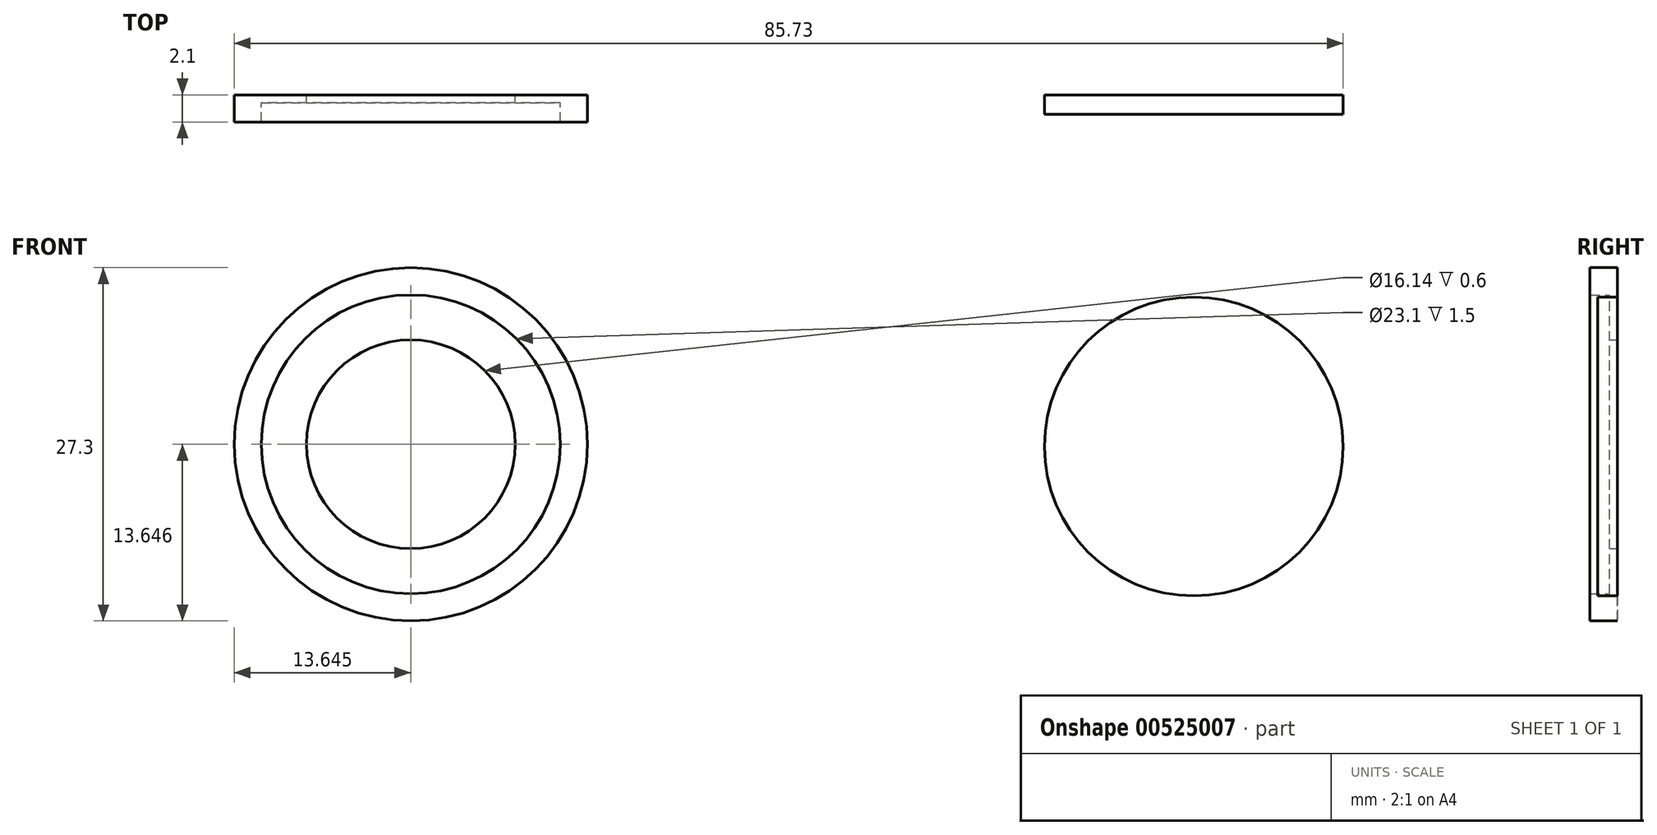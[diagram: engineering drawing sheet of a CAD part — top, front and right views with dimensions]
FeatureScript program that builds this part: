
annotation { "Feature Type Name" : "Feature", "Feature Type Description" : "" }
export const myFeature = defineFeature(function(context is Context, id is Id, definition is map)
    precondition{}
    {
        {
            var Q0;
            Q0=qCreatedBy(makeId("Front.planeOp"),FACE);
            var sketch = newSketch(context, id + "F0", { "sketchPlane" : qUnion([Q0])});
            skCircle(sketch, "E0", {"center": v(-41.74, 19.38) * mm, "radius": 13.65 * mm});
            skCircle(sketch, "E1", {"center": v(-41.74, 19.38) * mm, "radius": 11.55 * mm});
            skCircle(sketch, "E2", {"center": v(-41.74, 19.38) * mm, "radius": 8.07 * mm});
            skSolve(sketch);
        }
        {
            var Q0;
            Q0=makeQuery(id+"F0.imprint","IMPRINT",FACE,{"disambiguationData":[TD([[makeQuery(id+"F0.imprint","IMPRINT",EDGE,{"derivedFrom":sQuery(id+"F0.wireOp",EDGE,"E0")}),1.0]])]});
            var Q1;
            Q1=makeQuery(id+"F0.imprint","IMPRINT",FACE,{"disambiguationData":[TD([[makeQuery(id+"F0.imprint","IMPRINT",EDGE,{"derivedFrom":sQuery(id+"F0.wireOp",EDGE,"E1")}),1.0]])]});
            extrude(context, id + "F1", {"entities" : qUnion([Q0, Q1]), "depth" : 0.6 * mm, "offsetDistance" : 25 * mm});
        }
        {
            var Q0;
            Q0=makeQuery(id+"F0.imprint","IMPRINT",FACE,{"disambiguationData":[TD([[makeQuery(id+"F0.imprint","IMPRINT",EDGE,{"derivedFrom":sQuery(id+"F0.wireOp",EDGE,"E0")}),1.0]])]});
            extrude(context, id + "F2", {"entities" : qUnion([Q0]), "operationType" : NewBodyOperationType.ADD, "depth" : 2.1 * mm, "offsetDistance" : 25 * mm});
        }
        {
            var Q0;
            Q0=qCreatedBy(makeId("Front.planeOp"),FACE);
            var sketch = newSketch(context, id + "F3", { "sketchPlane" : qUnion([Q0])});
            skCircle(sketch, "E3", {"center": v(18.8, 19.2) * mm, "radius": 11.55 * mm});
            skSolve(sketch);
        }
        {
            var Q0;
            Q0=makeQuery(id+"F3.imprint","IMPRINT",FACE,{"disambiguationData":[TD([[makeQuery(id+"F3.imprint","IMPRINT",EDGE,{"derivedFrom":sQuery(id+"F3.wireOp",EDGE,"E3")}),1.0]])]});
            extrude(context, id + "F4", {"entities" : qUnion([Q0]), "depth" : 1.5 * mm, "offsetDistance" : 25 * mm});
        }
    });
